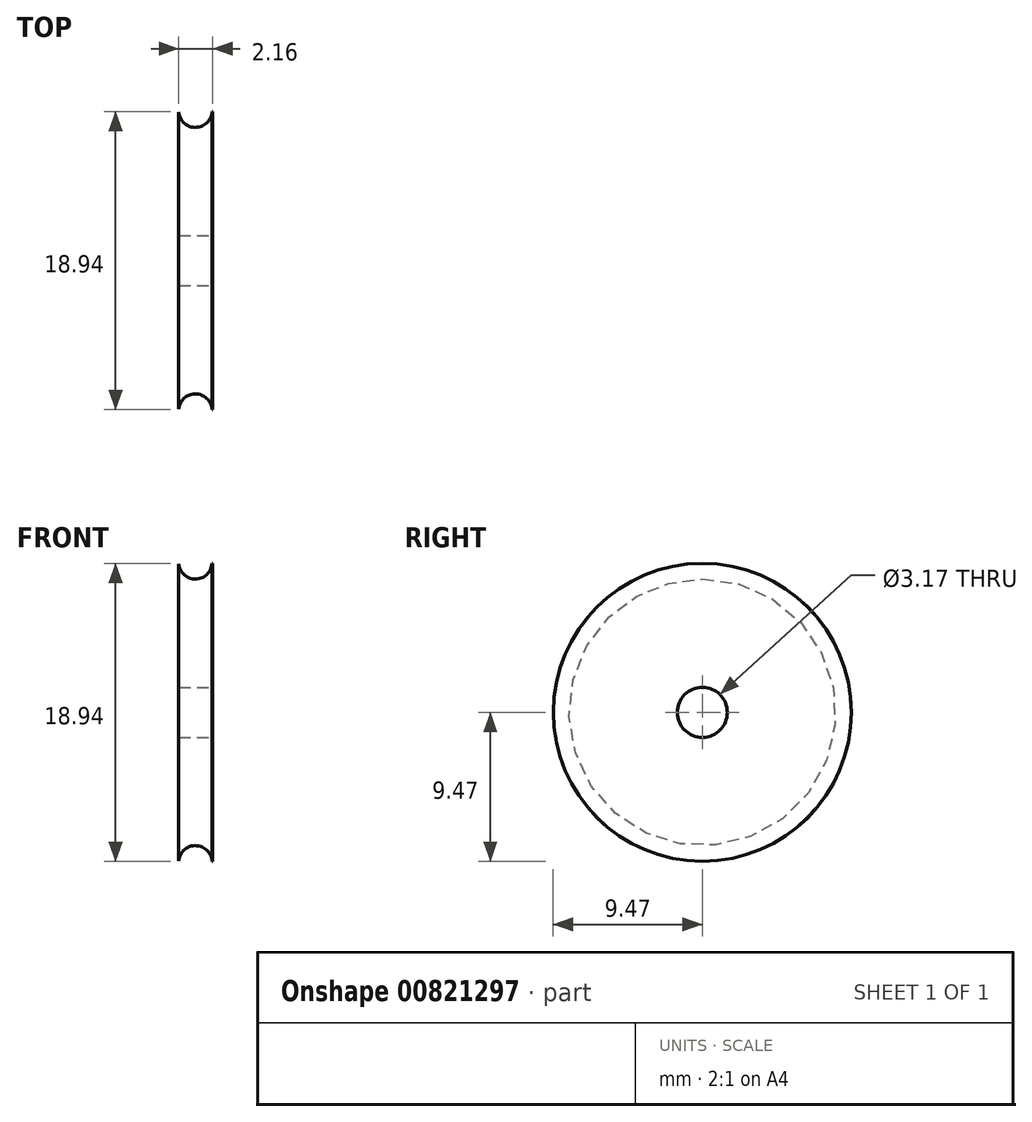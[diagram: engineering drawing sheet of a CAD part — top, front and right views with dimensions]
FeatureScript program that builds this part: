
annotation { "Feature Type Name" : "Feature", "Feature Type Description" : "" }
export const myFeature = defineFeature(function(context is Context, id is Id, definition is map)
    precondition{}
    {
        {
            var Q0;
            Q0=qCreatedBy(makeId("Front.planeOp"),FACE);
            var sketch = newSketch(context, id + "F0", { "sketchPlane" : qUnion([Q0])});
            skCircle(sketch, "E0", {"center": v(0, 0) * mm, "radius": 9.53 * mm});
            skLineSegment(sketch, "E1", {"start": v(-1.06, 0) * mm, "end": v(1.1, 0) * mm});
            skLineSegment(sketch, "E2", {"start": v(-1.06, 0) * mm, "end": v(-1.06, 9.47) * mm});
            skLineSegment(sketch, "E3", {"start": v(1.1, 0) * mm, "end": v(1.1, 9.46) * mm});
            skCircle(sketch, "E4", {"center": v(0, 9.53) * mm, "radius": 1.06 * mm});
            skSolve(sketch);
        }
        {
            var Q0;
            {var subQ1=sQuery(id+"F0.wireOp",EDGE,"E1");Q0=makeQuery(id+"F0.imprint","IMPRINT",FACE,{"disambiguationData":[TD([[makeQuery(id+"F0.imprint","IMPRINT",EDGE,{"derivedFrom":subQ1}),1.0]])]});}
            var Q1;
            Q1=sQuery(id+"F0.wireOp",EDGE,"E1");
            revolve(context, id + "F1", {"surfaceOperationType" : NewSurfaceOperationType.NEW, "entities" : qUnion([Q0]), "axis" : qUnion([Q1]), "revolveType" : RevolveType.FULL});
        }
        {
            var Q0;
            Q0=qCreatedBy(makeId("Right.planeOp"),FACE);
            var sketch = newSketch(context, id + "F2", { "sketchPlane" : qUnion([Q0])});
            skCircle(sketch, "E5", {"center": v(0, 0) * mm, "radius": 1.59 * mm});
            skSolve(sketch);
        }
        {
            var Q0;
            Q0=qSketchRegion(id+"F2",true);
            extrude(context, id + "F3", {"entities" : qUnion([Q0]), "operationType" : NewBodyOperationType.REMOVE, "oppositeDirection" : true, "depth" : 25.4 * mm, "offsetDistance" : 25.4 * mm, "hasSecondDirection" : true, "secondDirectionOppositeDirection" : false, "secondDirectionDepth" : 25.4 * mm});
        }
    });
